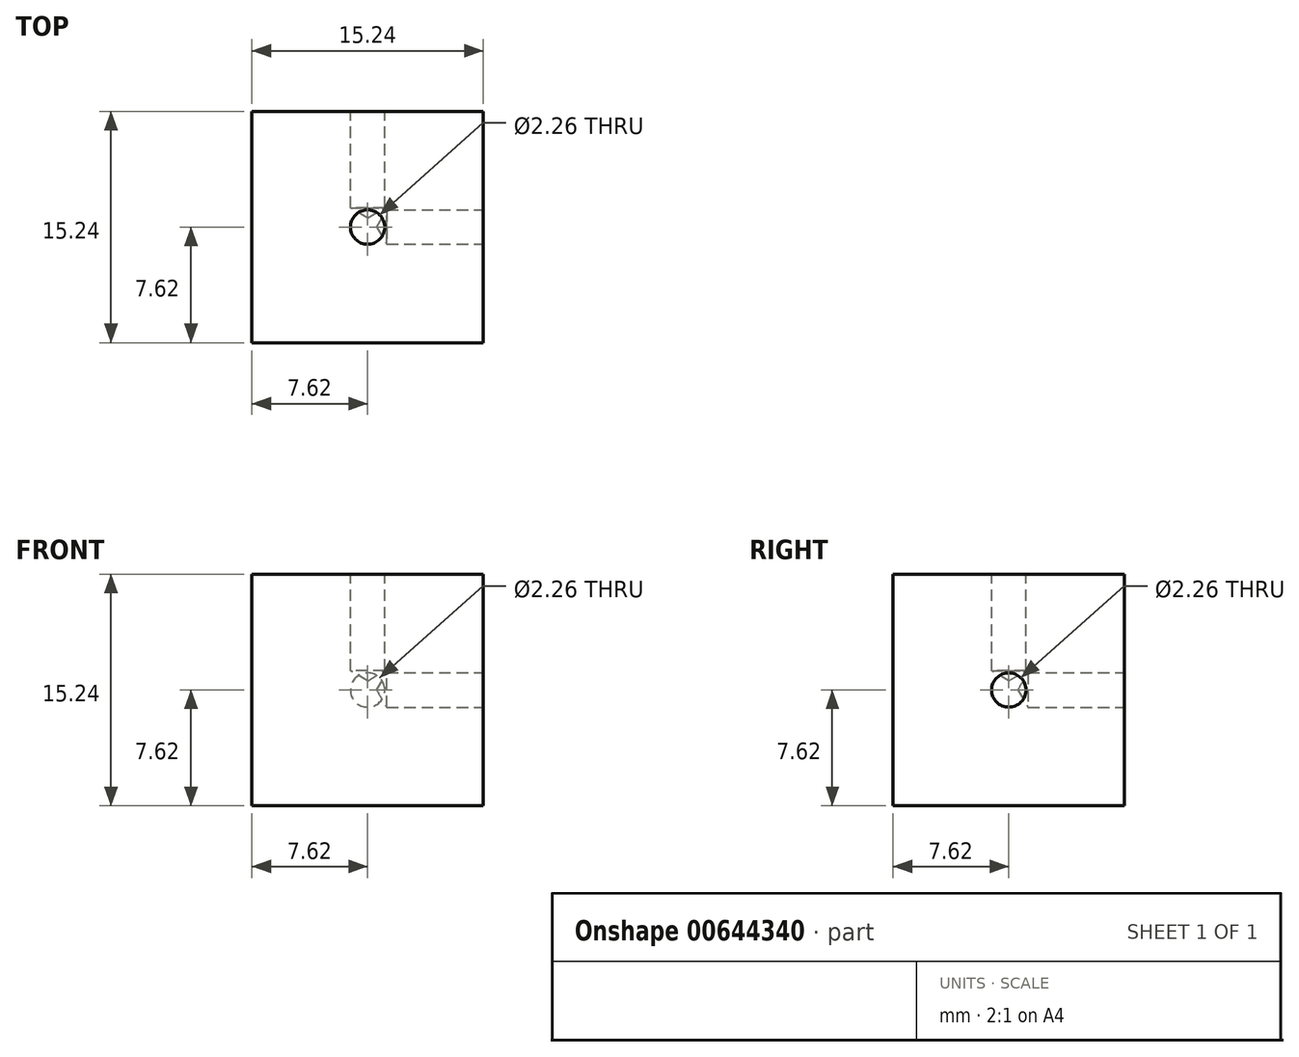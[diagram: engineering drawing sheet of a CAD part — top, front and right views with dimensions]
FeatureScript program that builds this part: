
annotation { "Feature Type Name" : "Feature", "Feature Type Description" : "" }
export const myFeature = defineFeature(function(context is Context, id is Id, definition is map)
    precondition{}
    {
        {
            var Q0;
            Q0=qCreatedBy(makeId("Top.planeOp"),FACE);
            var sketch = newSketch(context, id + "F0", { "sketchPlane" : qUnion([Q0])});
            skLineSegment(sketch, "E0.bottom", {"start": v(7.62, 7.62) * mm, "end": v(-7.62, 7.62) * mm});
            skLineSegment(sketch, "E0.top", {"start": v(7.62, -7.62) * mm, "end": v(-7.62, -7.62) * mm});
            skLineSegment(sketch, "E0.left", {"start": v(7.62, 7.62) * mm, "end": v(7.62, -7.62) * mm});
            skLineSegment(sketch, "E0.right", {"start": v(-7.62, 7.62) * mm, "end": v(-7.62, -7.62) * mm});
            skPoint(sketch, "E0.middle", {"position": v(0, 0) * mm});
            skSolve(sketch);
        }
        {
            var Q0;
            Q0 = qSketchRegion(id + "F0", true);
            extrude(context, id + "F1", {"entities" : qUnion([Q0]), "endBound" : BoundingType.SYMMETRIC, "depth" : 15.24 * mm, "offsetDistance" : 25.4 * mm});
        }
        {
            var Q0;
            Q0=makeQuery(id+"F1.opExtrude","SWEPT_FACE",FACE,{"disambiguationData":[OSD([sQuery(id+"F0.wireOp",EDGE,"E0.left")])]});
            var sketch = newSketch(context, id + "F2", { "sketchPlane" : qUnion([Q0])});
            skPoint(sketch, "E1", {"position": v(0, 0) * mm});
            skSolve(sketch);
        }
        {
            var Q0;
            Q0=sQuery(id+"F2.wireOp",VERTEX,"E1");
            var Q1;
            Q1=makeQuery(id+"F1.opExtrude","SWEPT_BODY",BODY,{"disambiguationData":[OSD([sQuery(id+"F0.wireOp",EDGE,"E0.bottom"),sQuery(id+"F0.wireOp",EDGE,"E0.top"),sQuery(id+"F0.wireOp",EDGE,"E0.left"),sQuery(id+"F0.wireOp",EDGE,"E0.right")])]});
            hole(context, id + "F3", {"style" : HoleStyle.SIMPLE, "endStyle" : HoleEndStyle.BLIND, "standardTappedOrClearance" : lookupTablePath({ "standard" : "ANSI", "engagement" : "75%", "pitch" : "40 tpi", "size" : "#4", "type" : "Tapped" }), "standardBlindInLast" : lookupTablePath({ "standard" : "ANSI", "engagement" : "75%", "pitch" : "40 tpi", "size" : "#4", "type" : "Tapped" }), "holeDiameter" : 2.26 * mm, "majorDiameter" : 2.84 * mm, "showTappedDepth" : true, "holeDepth" : 6.35 * mm, "isTappedThrough" : true, "tappedDepth" : 4.44 * mm, "tapClearance" : 3, "locations" : qUnion([Q0]), "scope" : qUnion([Q1])});
        }
        {
            var Q0;
            Q0=makeQuery(id+"F1.opExtrude","SWEPT_FACE",FACE,{"disambiguationData":[OSD([sQuery(id+"F0.wireOp",EDGE,"E0.bottom")])]});
            var sketch = newSketch(context, id + "F4", { "sketchPlane" : qUnion([Q0])});
            skPoint(sketch, "E2", {"position": v(0, 0) * mm});
            skSolve(sketch);
        }
        {
            var Q0;
            Q0=makeQuery(id+"F1.opExtrude","CAP_FACE",FACE,{"disambiguationData":[OSD([sQuery(id+"F0.wireOp",EDGE,"E0.bottom"),sQuery(id+"F0.wireOp",EDGE,"E0.top"),sQuery(id+"F0.wireOp",EDGE,"E0.left"),sQuery(id+"F0.wireOp",EDGE,"E0.right")])],"isStart":false});
            var sketch = newSketch(context, id + "F5", { "sketchPlane" : qUnion([Q0])});
            skPoint(sketch, "E3", {"position": v(0, 0) * mm});
            skSolve(sketch);
        }
        {
            var Q0;
            Q0=sQuery(id+"F5.wireOp",VERTEX,"E3");
            var Q1;
            Q1=makeQuery(id+"F1.opExtrude","SWEPT_BODY",BODY,{"disambiguationData":[OSD([sQuery(id+"F0.wireOp",EDGE,"E0.bottom"),sQuery(id+"F0.wireOp",EDGE,"E0.top"),sQuery(id+"F0.wireOp",EDGE,"E0.left"),sQuery(id+"F0.wireOp",EDGE,"E0.right")])]});
            hole(context, id + "F6", {"style" : HoleStyle.SIMPLE, "endStyle" : HoleEndStyle.BLIND, "standardTappedOrClearance" : lookupTablePath({ "standard" : "ANSI", "engagement" : "75%", "pitch" : "40 tpi", "size" : "#4", "type" : "Tapped" }), "standardBlindInLast" : lookupTablePath({ "standard" : "ANSI", "engagement" : "75%", "pitch" : "40 tpi", "size" : "#4", "type" : "Tapped" }), "holeDiameter" : 2.26 * mm, "majorDiameter" : 2.84 * mm, "showTappedDepth" : true, "holeDepth" : 6.35 * mm, "isTappedThrough" : true, "tappedDepth" : 4.44 * mm, "tapClearance" : 3, "locations" : qUnion([Q0]), "scope" : qUnion([Q1])});
        }
        {
            var Q0;
            Q0=sQuery(id+"F4.wireOp",VERTEX,"E2");
            var Q1;
            Q1=makeQuery(id+"F1.opExtrude","SWEPT_BODY",BODY,{"disambiguationData":[OSD([sQuery(id+"F0.wireOp",EDGE,"E0.bottom"),sQuery(id+"F0.wireOp",EDGE,"E0.top"),sQuery(id+"F0.wireOp",EDGE,"E0.left"),sQuery(id+"F0.wireOp",EDGE,"E0.right")])]});
            hole(context, id + "F7", {"style" : HoleStyle.SIMPLE, "endStyle" : HoleEndStyle.BLIND, "standardTappedOrClearance" : lookupTablePath({ "standard" : "ANSI", "engagement" : "75%", "pitch" : "40 tpi", "size" : "#4", "type" : "Tapped" }), "standardBlindInLast" : lookupTablePath({ "standard" : "ANSI", "engagement" : "75%", "pitch" : "40 tpi", "size" : "#4", "type" : "Tapped" }), "holeDiameter" : 2.26 * mm, "majorDiameter" : 2.84 * mm, "showTappedDepth" : true, "holeDepth" : 6.35 * mm, "isTappedThrough" : true, "tappedDepth" : 4.44 * mm, "tapClearance" : 3, "locations" : qUnion([Q0]), "scope" : qUnion([Q1])});
        }
    });
